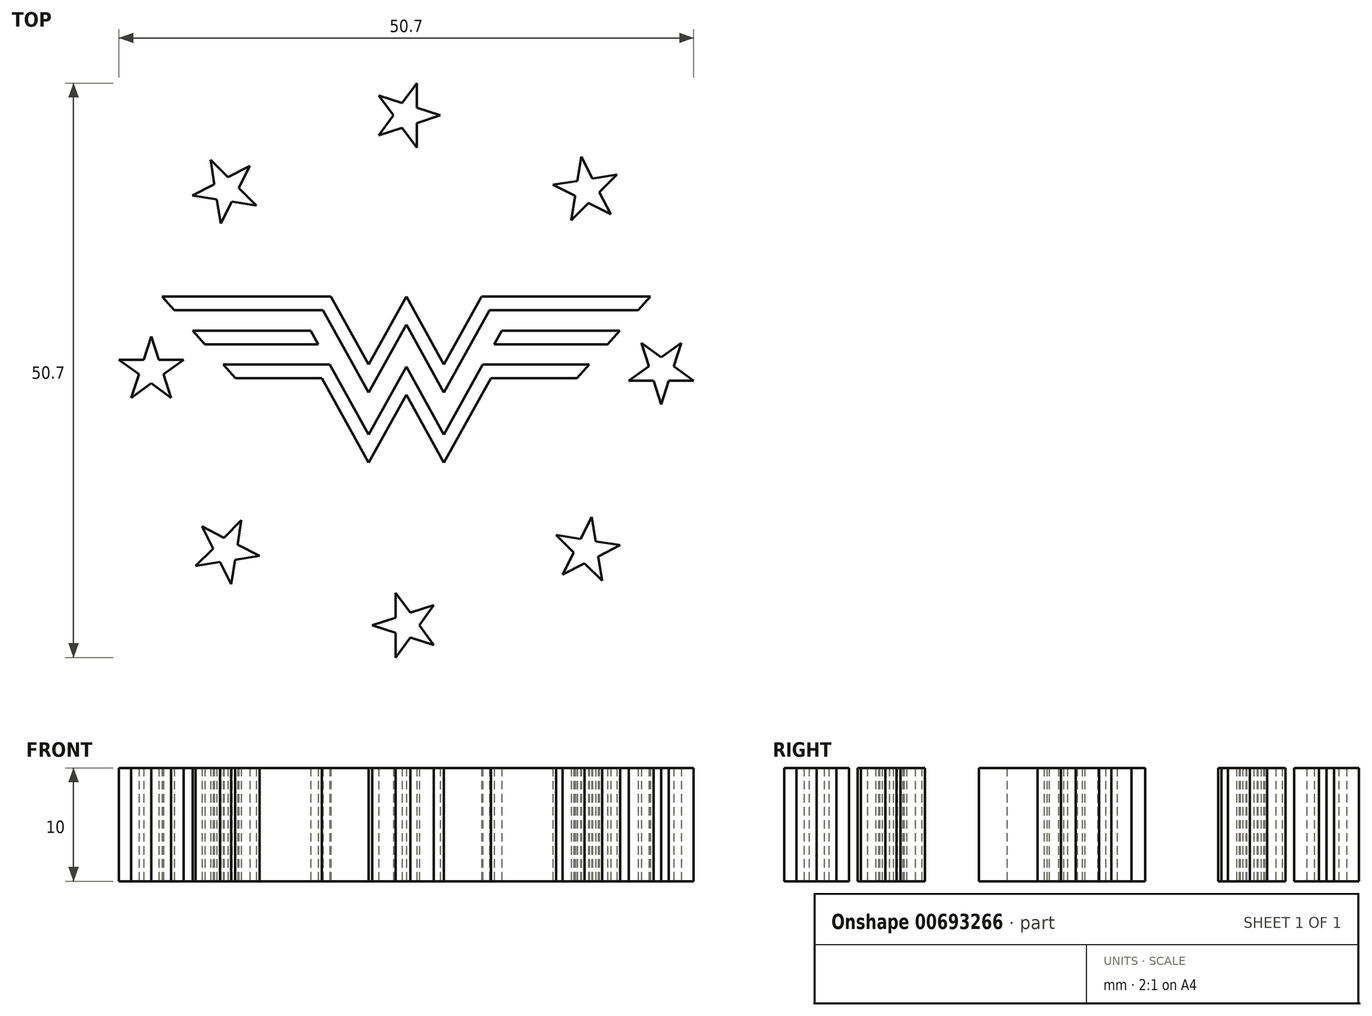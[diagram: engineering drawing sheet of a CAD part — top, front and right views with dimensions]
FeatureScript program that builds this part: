
annotation { "Feature Type Name" : "Feature", "Feature Type Description" : "" }
export const myFeature = defineFeature(function(context is Context, id is Id, definition is map)
    precondition{}
    {
        {
            var Q0;
            Q0=qCreatedBy(makeId("Right.planeOp"),FACE);
            var sketch = newSketch(context, id + "F0", { "sketchPlane" : qUnion([Q0])});
            skLineSegment(sketch, "E0", {"start": v(0, 10) * mm, "end": v(0, -10) * mm, "construction": true});
            skSolve(sketch);
        }
        {
            var Q0;
            Q0=qCreatedBy(makeId("Top.planeOp"),FACE);
            var sketch = newSketch(context, id + "F1", { "sketchPlane" : qUnion([Q0])});
            skCircle(sketch, "E1", {"center": v(0, 0) * mm, "radius": 22.5 * mm, "construction": true});
            skCircle(sketch, "E2", {"center": v(-22.5, 0) * mm, "radius": 3 * mm, "construction": true});
            skLineSegment(sketch, "E3", {"start": v(-20.74, -2.43) * mm, "end": v(-25.35, 0.93) * mm});
            skLineSegment(sketch, "E4", {"start": v(-25.35, 0.93) * mm, "end": v(-19.65, 0.93) * mm});
            skLineSegment(sketch, "E5", {"start": v(-19.65, 0.93) * mm, "end": v(-24.26, -2.43) * mm});
            skLineSegment(sketch, "E6", {"start": v(-24.26, -2.43) * mm, "end": v(-22.5, 3) * mm});
            skLineSegment(sketch, "E7", {"start": v(-22.5, 3) * mm, "end": v(-20.74, -2.43) * mm});
            skSolve(sketch);
        }
        {
            var Q0;
            Q0=qCreatedBy(makeId("Top.planeOp"),FACE);
            var sketch = newSketch(context, id + "F2", { "sketchPlane" : qUnion([Q0])});
            skLineSegment(sketch, "E8", {"start": v(-21.54, 6.5) * mm, "end": v(-6.65, 6.5) * mm});
            skLineSegment(sketch, "E9", {"start": v(-6.65, 6.5) * mm, "end": v(-3.33, 0.5) * mm});
            skLineSegment(sketch, "E10", {"start": v(-3.33, 0.5) * mm, "end": v(0, 6.5) * mm});
            skLineSegment(sketch, "E11", {"start": v(0, 6.5) * mm, "end": v(0, -8.16) * mm, "construction": true});
            skLineSegment(sketch, "E12", {"start": v(-20.46, 5.3) * mm, "end": v(-7.36, 5.3) * mm});
            skLineSegment(sketch, "E13", {"start": v(-7.36, 5.3) * mm, "end": v(-3.33, -1.98) * mm});
            skLineSegment(sketch, "E14", {"start": v(-3.33, -1.98) * mm, "end": v(0, 4.02) * mm});
            skLineSegment(sketch, "E15", {"start": v(-18.84, 3.5) * mm, "end": v(-8.42, 3.5) * mm});
            skLineSegment(sketch, "E16", {"start": v(-8.42, 3.5) * mm, "end": v(-7.75, 2.3) * mm});
            skLineSegment(sketch, "E17", {"start": v(-7.75, 2.3) * mm, "end": v(-17.76, 2.3) * mm});
            skLineSegment(sketch, "E18", {"start": v(-17.76, 2.3) * mm, "end": v(-18.84, 3.5) * mm});
            skLineSegment(sketch, "E19", {"start": v(0, 4.02) * mm, "end": v(0, 6.5) * mm});
            skLineSegment(sketch, "E20", {"start": v(-16.14, 0.5) * mm, "end": v(-15.06, -0.7) * mm});
            skLineSegment(sketch, "E21", {"start": v(-15.06, -0.7) * mm, "end": v(-7.46, -0.7) * mm});
            skLineSegment(sketch, "E22", {"start": v(-7.46, -0.7) * mm, "end": v(-3.33, -8.16) * mm});
            skLineSegment(sketch, "E23", {"start": v(-3.33, -8.16) * mm, "end": v(0, -2.16) * mm});
            skLineSegment(sketch, "E24", {"start": v(0, -2.16) * mm, "end": v(0, 0.31) * mm});
            skLineSegment(sketch, "E25", {"start": v(0, 0.31) * mm, "end": v(-3.33, -5.69) * mm});
            skLineSegment(sketch, "E26", {"start": v(-3.33, -5.69) * mm, "end": v(-6.76, 0.5) * mm});
            skLineSegment(sketch, "E27", {"start": v(-6.76, 0.5) * mm, "end": v(-16.14, 0.5) * mm});
            skLineSegment(sketch, "E28", {"start": v(-3.33, 0.5) * mm, "end": v(-2.28, -0.08) * mm, "construction": true});
            skLineSegment(sketch, "E29", {"start": v(-3.33, 0.5) * mm, "end": v(-4.38, -0.08) * mm, "construction": true});
            skPoint(sketch, "E30.startSnap0", {"position": v(-13.63, 3.5) * mm});
            skLineSegment(sketch, "E31", {"start": v(-14.1, 6.5) * mm, "end": v(-14.1, 5.3) * mm, "construction": true});
            skLineSegment(sketch, "E32", {"start": v(-20.46, 5.3) * mm, "end": v(-21.54, 6.5) * mm});
            skLineSegment(sketch, "E33", {"start": v(-13.63, 3.5) * mm, "end": v(-13.63, 2.3) * mm, "construction": true});
            skLineSegment(sketch, "E34", {"start": v(-11.26, 0.5) * mm, "end": v(-11.26, -0.7) * mm, "construction": true});
            skLineSegment(sketch, "E35", {"start": v(-3.33, -5.69) * mm, "end": v(-4.38, -6.27) * mm, "construction": true});
            skLineSegment(sketch, "E36", {"start": v(-3.33, -5.69) * mm, "end": v(-2.28, -6.27) * mm, "construction": true});
            skLineSegment(sketch, "E37", {"start": v(-3.33, -1.98) * mm, "end": v(-4.9, -2.85) * mm, "construction": true});
            skLineSegment(sketch, "E38", {"start": v(-11.26, 0.5) * mm, "end": v(-11.26, 2.3) * mm, "construction": true});
            skLineSegment(sketch, "E39", {"start": v(-14.1, 5.3) * mm, "end": v(-14.1, 3.5) * mm, "construction": true});
            skSolve(sketch);
        }
        {
            var Q0;
            Q0 = qSketchRegion(id + "F2", true);
            extrude(context, id + "F3", {"entities" : qUnion([Q0]), "endBound" : BoundingType.SYMMETRIC, "depth" : 10 * mm, "offsetDistance" : 25 * mm});
        }
        {
            var Q0;
            Q0=makeQuery(id+"F3.opExtrude","SWEPT_BODY",BODY,{"disambiguationData":[OSD([sQuery(id+"F2.wireOp",EDGE,"E8"),sQuery(id+"F2.wireOp",EDGE,"E9"),sQuery(id+"F2.wireOp",EDGE,"E10"),sQuery(id+"F2.wireOp",EDGE,"E12"),sQuery(id+"F2.wireOp",EDGE,"E13"),sQuery(id+"F2.wireOp",EDGE,"E14"),sQuery(id+"F2.wireOp",EDGE,"E19"),sQuery(id+"F2.wireOp",EDGE,"E32")])]});
            var Q1;
            Q1=makeQuery(id+"F3.opExtrude","SWEPT_BODY",BODY,{"disambiguationData":[OSD([sQuery(id+"F2.wireOp",EDGE,"E15"),sQuery(id+"F2.wireOp",EDGE,"E16"),sQuery(id+"F2.wireOp",EDGE,"E17"),sQuery(id+"F2.wireOp",EDGE,"E18")])]});
            var Q2;
            Q2=makeQuery(id+"F3.opExtrude","SWEPT_BODY",BODY,{"disambiguationData":[OSD([sQuery(id+"F2.wireOp",EDGE,"E20"),sQuery(id+"F2.wireOp",EDGE,"E21"),sQuery(id+"F2.wireOp",EDGE,"E22"),sQuery(id+"F2.wireOp",EDGE,"E23"),sQuery(id+"F2.wireOp",EDGE,"E24"),sQuery(id+"F2.wireOp",EDGE,"E25"),sQuery(id+"F2.wireOp",EDGE,"E26"),sQuery(id+"F2.wireOp",EDGE,"E27")])]});
            var Q3;
            Q3=qCreatedBy(makeId("Right.planeOp"),FACE);
            mirror(context, id + "F4", {"operationType" : NewBodyOperationType.ADD, "entities" : qUnion([Q0, Q1, Q2]), "mirrorPlane" : qUnion([Q3])});
        }
        {
            var Q0;
            {var subQ1=sQuery(id+"F1.wireOp",EDGE,"E3");var subQ5=sQuery(id+"F1.wireOp",EDGE,"E5");var subQ6=makeQuery(id+"F1.imprint","INTERSECT",VERTEX,{"derivedFrom":[subQ1,subQ5]});Q0=makeQuery(id+"F1.imprint","IMPRINT",FACE,{"disambiguationData":[TD([[makeQuery(id+"F1.imprint","IMPRINT",EDGE,{"disambiguationData":[TD([[subQ6,-1.0]])],"derivedFrom":subQ1}),-1.0]])]});}
            var Q1;
            {var subQ0=sQuery(id+"F1.wireOp",EDGE,"E6");var subQ1=sQuery(id+"F1.wireOp",EDGE,"E4");var subQ2=makeQuery(id+"F1.imprint","INTERSECT",VERTEX,{"derivedFrom":[subQ1,subQ0]});Q1=makeQuery(id+"F1.imprint","IMPRINT",FACE,{"disambiguationData":[TD([[makeQuery(id+"F1.imprint","IMPRINT",EDGE,{"disambiguationData":[TD([[subQ2,-1.0]])],"derivedFrom":subQ1}),1.0]])]});}
            var Q2;
            {var subQ0=sQuery(id+"F1.wireOp",EDGE,"E4");var subQ1=sQuery(id+"F1.wireOp",EDGE,"E3");var subQ2=makeQuery(id+"F1.imprint","INTERSECT",VERTEX,{"derivedFrom":[subQ1,subQ0]});Q2=makeQuery(id+"F1.imprint","IMPRINT",FACE,{"disambiguationData":[TD([[makeQuery(id+"F1.imprint","IMPRINT",EDGE,{"disambiguationData":[TD([[subQ2,1.0]])],"derivedFrom":subQ1}),-1.0]])]});}
            var Q3;
            {var subQ0=sQuery(id+"F1.wireOp",EDGE,"E5");var subQ1=sQuery(id+"F1.wireOp",EDGE,"E3");var subQ2=makeQuery(id+"F1.imprint","INTERSECT",VERTEX,{"derivedFrom":[subQ1,subQ0]});Q3=makeQuery(id+"F1.imprint","IMPRINT",FACE,{"disambiguationData":[TD([[makeQuery(id+"F1.imprint","IMPRINT",EDGE,{"disambiguationData":[TD([[subQ2,-1.0]])],"derivedFrom":subQ1}),1.0]])]});}
            var Q4;
            {var subQ0=sQuery(id+"F1.wireOp",EDGE,"E7");var subQ1=sQuery(id+"F1.wireOp",EDGE,"E3");var subQ2=makeQuery(id+"F1.imprint","INTERSECT",VERTEX,{"derivedFrom":[subQ1,subQ0]});Q4=makeQuery(id+"F1.imprint","IMPRINT",FACE,{"disambiguationData":[TD([[makeQuery(id+"F1.imprint","IMPRINT",EDGE,{"disambiguationData":[TD([[subQ2,-1.0]])],"derivedFrom":subQ1}),-1.0]])]});}
            var Q5;
            {var subQ0=sQuery(id+"F1.wireOp",EDGE,"E5");var subQ1=sQuery(id+"F1.wireOp",EDGE,"E4");var subQ2=makeQuery(id+"F1.imprint","INTERSECT",VERTEX,{"derivedFrom":[subQ1,subQ0]});Q5=makeQuery(id+"F1.imprint","IMPRINT",FACE,{"disambiguationData":[TD([[makeQuery(id+"F1.imprint","IMPRINT",EDGE,{"disambiguationData":[TD([[subQ2,1.0]])],"derivedFrom":subQ1}),-1.0]])]});}
            extrude(context, id + "F5", {"entities" : qUnion([Q0, Q1, Q2, Q3, Q4, Q5]), "endBound" : BoundingType.SYMMETRIC, "depth" : 10 * mm, "offsetDistance" : 25 * mm});
        }
        {
            var Q0;
            Q0=makeQuery(id+"F5.opExtrude","SWEPT_BODY",BODY,{"disambiguationData":[OSD([sQuery(id+"F1.wireOp",EDGE,"E3"),sQuery(id+"F1.wireOp",EDGE,"E4"),sQuery(id+"F1.wireOp",EDGE,"E5"),sQuery(id+"F1.wireOp",EDGE,"E6"),sQuery(id+"F1.wireOp",EDGE,"E7")])]});
            var Q1;
            Q1=sQuery(id+"F0.wireOp",EDGE,"E0");
            circularPattern(context, id + "F6", {"entities" : qUnion([Q0]), "axis" : qUnion([Q1]), "angle" : 360 * degree, "instanceCount" : 8, "equalSpace" : true});
        }
    });
